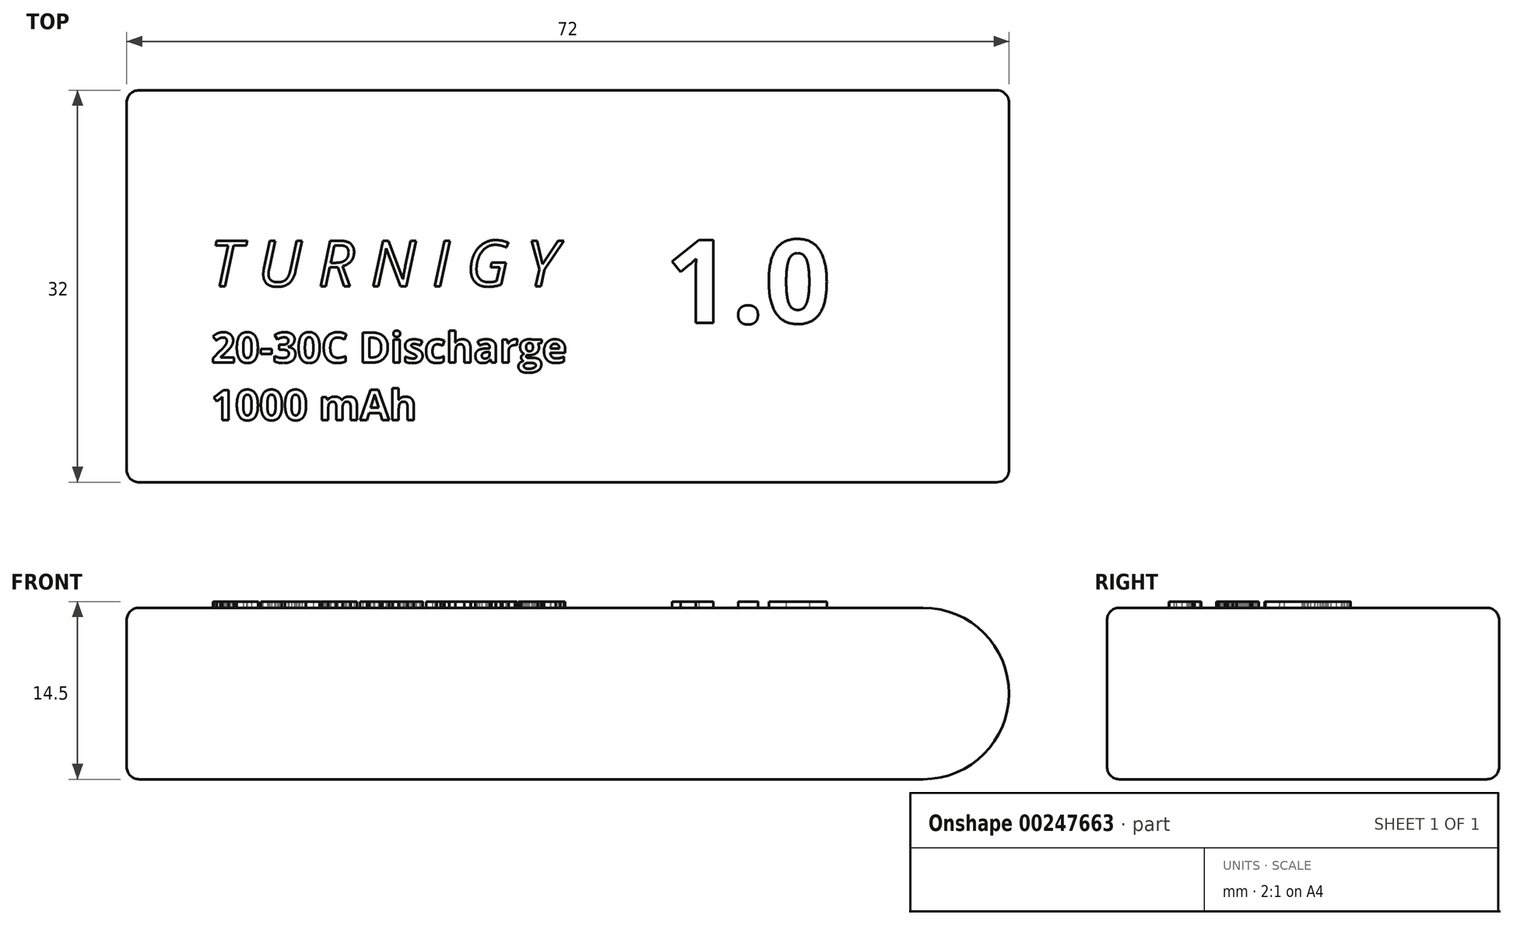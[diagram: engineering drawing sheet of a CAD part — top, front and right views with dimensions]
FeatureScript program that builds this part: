
annotation { "Feature Type Name" : "Feature", "Feature Type Description" : "" }
export const myFeature = defineFeature(function(context is Context, id is Id, definition is map)
    precondition{}
    {
        {
            var Q0;
            Q0=qCreatedBy(makeId("Front.planeOp"),FACE);
            var sketch = newSketch(context, id + "F0", { "sketchPlane" : qUnion([Q0])});
            skLineSegment(sketch, "E0.bottom", {"start": v(36, 7) * mm, "end": v(-36, 7) * mm});
            skLineSegment(sketch, "E0.top", {"start": v(36, -7) * mm, "end": v(-36, -7) * mm});
            skLineSegment(sketch, "E0.left", {"start": v(36, 7) * mm, "end": v(36, -7) * mm});
            skLineSegment(sketch, "E0.right", {"start": v(-36, 7) * mm, "end": v(-36, -7) * mm});
            skPoint(sketch, "E0.middle", {"position": v(0, 0) * mm});
            skSolve(sketch);
        }
        {
            var Q0;
            Q0=makeQuery(id+"F0.imprint","IMPRINT",FACE,{"disambiguationData":[TD([[makeQuery(id+"F0.imprint","IMPRINT",EDGE,{"derivedFrom":sQuery(id+"F0.wireOp",EDGE,"E0.bottom")}),1.0]])]});
            extrude(context, id + "F1", {"entities" : qUnion([Q0]), "depth" : 32 * mm, "symmetric" : true});
        }
        {
            var Q0;
            Q0=makeQuery(id+"F1.opExtrude","SWEPT_EDGE",EDGE,{"disambiguationData":[OSD([sQuery(id+"F0.wireOp",EDGE,"E0.bottom"),sQuery(id+"F0.wireOp",EDGE,"E0.left")])]});
            var Q1;
            Q1=makeQuery(id+"F1.opExtrude","SWEPT_EDGE",EDGE,{"disambiguationData":[OSD([sQuery(id+"F0.wireOp",EDGE,"E0.top"),sQuery(id+"F0.wireOp",EDGE,"E0.left")])]});
            fillet(context, id + "F2", {"entities" : qUnion([Q0, Q1]), "radius" : 7 * mm, "tangentPropagation" : true, "allowEdgeOverflow" : false});
        }
        {
            var Q0;
            Q0=makeQuery(id+"F1.opExtrude","CAP_EDGE",EDGE,{"disambiguationData":[OSD([sQuery(id+"F0.wireOp",EDGE,"E0.bottom")])],"isStart":false});
            var Q1;
            Q1=makeQuery(id+"F1.opExtrude","CAP_EDGE",EDGE,{"disambiguationData":[OSD([sQuery(id+"F0.wireOp",EDGE,"E0.bottom")])],"isStart":true});
            var Q2;
            Q2=makeQuery(id+"F1.opExtrude","SWEPT_EDGE",EDGE,{"disambiguationData":[OSD([sQuery(id+"F0.wireOp",EDGE,"E0.top"),sQuery(id+"F0.wireOp",EDGE,"E0.right")])]});
            var Q3;
            Q3=makeQuery(id+"F1.opExtrude","CAP_EDGE",EDGE,{"disambiguationData":[OSD([sQuery(id+"F0.wireOp",EDGE,"E0.right")])],"isStart":true});
            var Q4;
            Q4=makeQuery(id+"F1.opExtrude","CAP_EDGE",EDGE,{"disambiguationData":[OSD([sQuery(id+"F0.wireOp",EDGE,"E0.right")])],"isStart":false});
            fillet(context, id + "F3", {"entities" : qUnion([Q0, Q1, Q2, Q3, Q4]), "radius" : 1 * mm, "tangentPropagation" : true, "allowEdgeOverflow" : false});
        }
        {
            var Q0;
            Q0=makeQuery(id+"F1.opExtrude","SWEPT_EDGE",EDGE,{"disambiguationData":[OSD([sQuery(id+"F0.wireOp",EDGE,"E0.bottom"),sQuery(id+"F0.wireOp",EDGE,"E0.right")])]});
            fillet(context, id + "F4", {"entities" : qUnion([Q0]), "radius" : 1 * mm, "tangentPropagation" : true, "allowEdgeOverflow" : false});
        }
        {
            var Q0;
            Q0=makeQuery(id+"F1.opExtrude","SWEPT_FACE",FACE,{"disambiguationData":[OSD([sQuery(id+"F0.wireOp",EDGE,"E0.bottom")])]});
            var sketch = newSketch(context, id + "F5", { "sketchPlane" : qUnion([Q0])});
            skText(sketch, "E1", { "text": "T U R N I G Y", "fontName": "OpenSans-Italic.ttf"});
            skText(sketch, "E2", { "text": "20-30C Discharge\n1000 mAh", "fontName": "OpenSans-Bold.ttf"});
            skText(sketch, "E3", { "text": "1.0", "fontName": "OpenSans-Bold.ttf"});
            const initialGuessF5  = {"E1": [-0.02922, 0, 1, 0, 0.00375], "E2": [-0.0291, -0.00624, 1, 0, 0.00248], "E3": [0.00795, -0.003, 1, 0, 0.00682]};
            skSetInitialGuess(sketch, initialGuessF5);
            skSolve(sketch);
        }
        {
            var Q0;
            Q0 = qSketchRegion(id + "F5", true);
            extrude(context, id + "F6", {"entities" : qUnion([Q0]), "operationType" : NewBodyOperationType.ADD, "depth" : .5 * mm});
        }
    });
